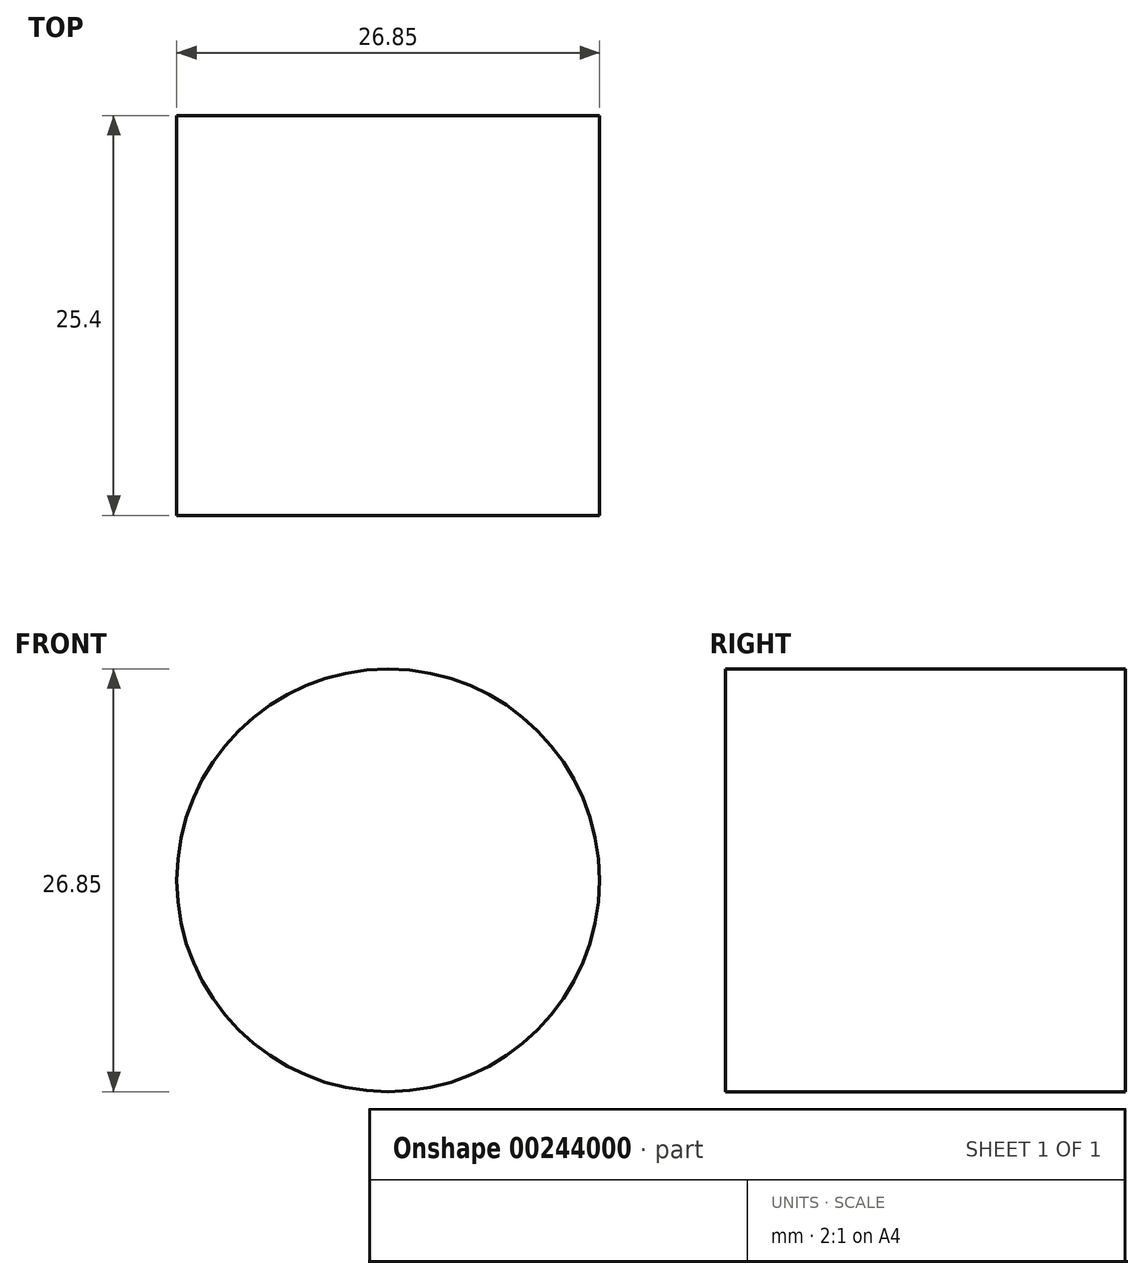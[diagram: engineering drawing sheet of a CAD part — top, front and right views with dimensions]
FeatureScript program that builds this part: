
annotation { "Feature Type Name" : "Feature", "Feature Type Description" : "" }
export const myFeature = defineFeature(function(context is Context, id is Id, definition is map)
    precondition{}
    {
        {
            var Q0;
            Q0=qCreatedBy(makeId("Front.planeOp"),FACE);
            var sketch = newSketch(context, id + "F0", { "sketchPlane" : qUnion([Q0])});
            skCircle(sketch, "E0", {"center": v(-33.42, 42.22) * mm, "radius": 7.33 * mm});
            skCircle(sketch, "E1", {"center": v(-14.37, 8.88) * mm, "radius": 13.42 * mm});
            skLineSegment(sketch, "E2", {"start": v(-27.72, 46.82) * mm, "end": v(-3.92, 17.31) * mm});
            skLineSegment(sketch, "E3", {"start": v(-40.27, 39.64) * mm, "end": v(-26.93, 4.16) * mm});
            skSolve(sketch);
        }
        {
            var Q0;
            {var subQ0=sQuery(id+"F0.wireOp",EDGE,"E1");var subQ1=makeQuery(id+"F0.imprint","INTERSECT",VERTEX,{"derivedFrom":[subQ0,sQuery(id+"F0.wireOp",EDGE,"E2")]});Q0=makeQuery(id+"F0.imprint","IMPRINT",FACE,{"disambiguationData":[TD([[makeQuery(id+"F0.imprint","IMPRINT",EDGE,{"disambiguationData":[TD([[subQ1,-1.0]])],"derivedFrom":subQ0}),1.0]])]});}
            extrude(context, id + "F1", {"entities" : qUnion([Q0]), "depth" : 25.4 * mm});
        }
    });
